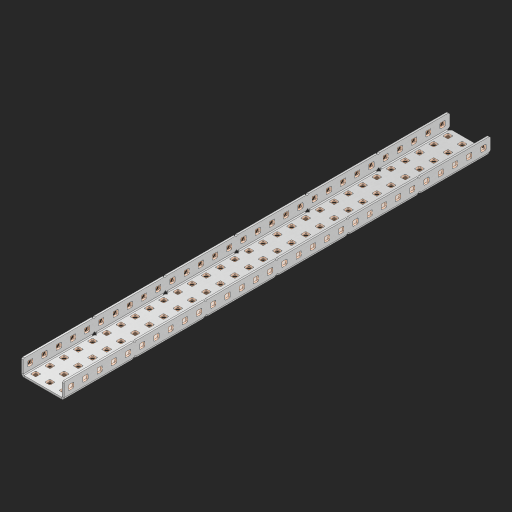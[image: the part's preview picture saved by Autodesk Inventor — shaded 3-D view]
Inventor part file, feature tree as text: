
AUTODESK INVENTOR PART (.ipt)
format: ipt  version: 2023 (Build 270158000, 158)  size: 1,831,424 bytes
history: native  units: in
note: dims shown in document units (in); Inventor stores cm internally (conversion verified against a paired STEP export)
features: other x155, extrude x149, sheet_metal_op x10, sketch x8, mirror x1, pattern_linear x1, chamfer x1
ambient origin geometry x8: Origin, YZ Plane, XZ Plane, XY Plane, X Axis, Y Axis, Z Axis, Center Point
bodies: Solid1 (feature_tree), Body (feature_tree)
feature tree (325):
  other  "Flange Pattern Plane"
  sheet_metal_op  "Flange Pattern"
  sheet_metal_op  "Body Pattern"
  other  "Arc Length"
  mirror  "Notch Mirror"
  pattern_linear  "Notch Pattern"  Spacing1=0.25in  [1 undecoded]
  chamfer  "End Chamfer"
  extrude  "Half Cut"  Depth=0.0625in
  sketch  "Sketch1"  dims[d0=1.5in]
  other  "Plate1"
  sketch  "Sketch2"  dims[d1=15.0in]
  other  "Plate2"
  sheet_metal_op  "Bend1"
  sheet_metal_op  "Corner1"
  sketch  "Sketch3"  dims[d2=0.0625in]
  other  "Flange Pattern Sketch"
  sketch  "Sketch7"  dims[d3=0.0625in]
  other  "Srf1"
  other  "Srf2"
  sketch  "Sketch8"  dims[d4=0.0312in]
  sketch  "Sketch9"  dims[d5=0.125in]
  other  "Srf91"
  sheet_metal_op  "Body Pattern Sketch"
  other  "Srf92"
  sketch  "Sketch13"  dims[d6=0.0625in]
  sketch  "Sketch14"  dims[d7=0.5in d8=90.0deg d9=0.0312in d10=0.25in d11=0.0625in d12=0.0625in d16=0.182in d17=0.02in d18=0.0625in d19=0.0in d20=0.25in d21=0.25in d46=0.172in d47=1.0in d48=0.0in d49=0.182in d50=0.02in d51=0.25in d52=0.25in d53=0.0625in d54=0.0in d55=0.172in d56=1.0in d57=0.0in d60=11.811in d62=0.5in d63=1.1811in d65=0.5in d85=0.1473in d86=0.1782in d88=0.04in d89=0.0625in d90=0.0in d91=0.04in d92=0.0491in d95=2.5in d96=0.04in d97=0.25in d98=45.0deg d101=0.0in d102=2.497in d131=1.5in d132=11.811in d134=0.5in d139=0.5in]
  other  "Srf856"
  other  "Srf1310"
  other  "Srf1311"
  other  "Srf1312"
  other  "Srf1376"
  other  "Srf1377"
  other  "Srf1728"
  other  "Srf1755"
  other  "Srf1878"
  other  "Srf1879"
  other  "Srf1880"
  other  "Srf1881"
  other  "Srf1882"
  other  "Srf1883"
  other  "Srf1884"
  other  "Srf1885"
  other  "Srf1886"
  other  "Srf1887"
  other  "Srf1888"
  other  "Srf1889"
  other  "Srf1890"
  other  "Srf1891"
  other  "Srf1892"
  other  "Srf1893"
  other  "Srf1894"
  other  "Srf1895"
  other  "Srf1896"
  other  "Srf1897"
  other  "Srf1898"
  other  "Srf1899"
  other  "Srf1900"
  other  "Srf1901"
  other  "Srf1902"
  other  "Srf1903"
  other  "Srf1904"
  other  "Srf1905"
  other  "Srf1906"
  other  "Srf1907"
  other  "Srf1908"
  other  "Srf1909"
  other  "Srf1910"
  other  "Srf1911"
  other  "Srf1912"
  other  "Srf1913"
  other  "Srf1914"
  other  "Srf1915"
  other  "Srf1916"
  other  "Srf1917"
  other  "Srf1918"
  other  "Srf1919"
  other  "Srf1920"
  other  "Srf1921"
  other  "Srf1922"
  other  "Srf1923"
  other  "Srf1924"
  other  "Srf1925"
  other  "Srf1926"
  other  "Srf1927"
  other  "Srf1928"
  other  "Srf1929"
  other  "Srf1930"
  other  "Srf1931"
  other  "Srf1942"
  other  "Srf1943"
  other  "Srf1944"
  other  "Srf1945"
  other  "Srf1946"
  other  "Srf1947"
  other  "Srf1948"
  other  "Srf1949"
  other  "Srf1950"
  other  "Srf1951"
  other  "Srf1952"
  other  "Srf1953"
  other  "Srf1954"
  other  "Srf1955"
  other  "Srf1956"
  other  "Srf1957"
  other  "Srf1958"
  other  "Srf1959"
  other  "Srf1960"
  other  "Srf1961"
  other  "Srf1962"
  other  "Srf1963"
  other  "Srf1964"
  other  "Srf1965"
  other  "Srf1966"
  other  "Srf1967"
  other  "Srf1968"
  other  "Srf1969"
  other  "Srf1970"
  other  "Srf1971"
  other  "Srf1972"
  other  "Srf1973"
  other  "Srf1974"
  other  "Srf1975"
  other  "Srf1976"
  other  "Srf1977"
  other  "Srf1978"
  other  "Srf1979"
  other  "Srf1980"
  other  "Srf1981"
  other  "Srf1982"
  other  "Srf1983"
  other  "Srf1984"
  other  "Srf1985"
  other  "Srf1986"
  other  "Srf1987"
  other  "Srf1988"
  other  "Srf1989"
  other  "Srf1990"
  other  "Srf1991"
  other  "Srf1992"
  other  "Srf1993"
  other  "Srf1994"
  other  "Srf1995"
  other  "Srf1996"
  other  "Srf1997"
  other  "Srf1998"
  other  "Srf1999"
  other  "Srf2000"
  other  "Srf2001"
  other  "Srf2002"
  other  "Srf2003"
  other  "Srf2004"
  other  "Srf2005"
  other  "Srf2006"
  other  "Srf2007"
  other  "Srf2008"
  other  "Srf2009"
  other  "Srf2010"
  other  "Srf2011"
  other  "Srf2012"
  other  "Srf2013"
  other  "Srf2014"
  other  "Srf2015"
  other  "Srf2016"
  other  "Srf2017"
  other  "Srf2018"
  other  "Srf2019"
  other  "Srf2020"
  other  "Srf2021"
  other  "Srf2022"
  other  "Srf2023"
  other  "Srf2024"
  other  "Srf2025"
  sheet_metal_op  "Flange Stamp"
  sheet_metal_op  "Flange Circle"
  sheet_metal_op  "Body Stamp"
  sheet_metal_op  "Body Circle"
  sheet_metal_op  "Notch"
  extrude  "ExtrusionSrf2"  Depth=0.0625in
  extrude  "ExtrusionSrf92"  Depth=1.5in
  extrude  "ExtrusionSrf856"  Depth=0.02in
  extrude  "ExtrusionSrf1310"  Depth=0.0625in
  extrude  "ExtrusionSrf1311"  TaperAngle=0.0deg  [1 undecoded]
  extrude  "ExtrusionSrf1312"  Depth=0.25in
  extrude  "ExtrusionSrf1376"  Depth=0.25in
  extrude  "ExtrusionSrf1377"  Depth=1.5in
  extrude  "ExtrusionSrf1728"  Depth=1.5in TaperAngle=0.0deg
  extrude  "ExtrusionSrf1755"  Depth=1.5in
  extrude  "ExtrusionSrf1878"  Depth=0.02in
  extrude  "ExtrusionSrf1879"  Depth=0.25in
  extrude  "ExtrusionSrf1880"  Depth=0.25in
  extrude  "ExtrusionSrf1881"  Depth=0.0625in
  extrude  "ExtrusionSrf1882"  TaperAngle=0.0deg  [1 undecoded]
  extrude  "ExtrusionSrf1883"  Depth=1.5in
  extrude  "ExtrusionSrf1884"  Depth=1.5in TaperAngle=0.0deg
  extrude  "ExtrusionSrf1885"  Depth=1.5in
  extrude  "ExtrusionSrf1886"  Depth=1.5in
  extrude  "ExtrusionSrf1887"  Depth=1.5in
  extrude  "ExtrusionSrf1888"  Depth=1.5in
  extrude  "ExtrusionSrf1889"  Depth=1.5in
  extrude  "ExtrusionSrf1890"  Depth=0.0625in
  extrude  "ExtrusionSrf1891"  TaperAngle=0.0deg  [1 undecoded]
  extrude  "ExtrusionSrf1892"  Depth=1.5in
  extrude  "ExtrusionSrf1893"  Depth=1.5in
  extrude  "ExtrusionSrf1894"  Depth=1.5in
  extrude  "ExtrusionSrf1895"  Depth=0.25in TaperAngle=45.0deg
  extrude  "ExtrusionSrf1896"  TaperAngle=0.0deg  [1 undecoded]
  extrude  "ExtrusionSrf1897"  Depth=1.5in
  extrude  "ExtrusionSrf1898"  Depth=1.5in
  extrude  "ExtrusionSrf1899"  Depth=1.5in
  extrude  "ExtrusionSrf1900"  Depth=1.5in
  extrude  "ExtrusionSrf1901"  Depth=1.5in
  extrude  "ExtrusionSrf1902"  [1 undecoded]
  extrude  "ExtrusionSrf1903"  [1 undecoded]
  extrude  "ExtrusionSrf1904"  [1 undecoded]
  extrude  "ExtrusionSrf1905"  [1 undecoded]
  extrude  "ExtrusionSrf1906"  [1 undecoded]
  extrude  "ExtrusionSrf1907"  [1 undecoded]
  extrude  "ExtrusionSrf1908"  [1 undecoded]
  extrude  "ExtrusionSrf1909"  [1 undecoded]
  extrude  "ExtrusionSrf1910"  [1 undecoded]
  extrude  "ExtrusionSrf1911"  [1 undecoded]
  extrude  "ExtrusionSrf1912"  [1 undecoded]
  extrude  "ExtrusionSrf1913"  [1 undecoded]
  extrude  "ExtrusionSrf1914"  [1 undecoded]
  extrude  "ExtrusionSrf1915"  [1 undecoded]
  extrude  "ExtrusionSrf1916"  [1 undecoded]
  extrude  "ExtrusionSrf1917"  [1 undecoded]
  extrude  "ExtrusionSrf1918"  [1 undecoded]
  extrude  "ExtrusionSrf1919"  [1 undecoded]
  extrude  "ExtrusionSrf1920"  [1 undecoded]
  extrude  "ExtrusionSrf1921"  [1 undecoded]
  extrude  "ExtrusionSrf1922"  [1 undecoded]
  extrude  "ExtrusionSrf1923"  [1 undecoded]
  extrude  "ExtrusionSrf1924"  [1 undecoded]
  extrude  "ExtrusionSrf1925"  [1 undecoded]
  extrude  "ExtrusionSrf1926"  [1 undecoded]
  extrude  "ExtrusionSrf1927"  [1 undecoded]
  extrude  "ExtrusionSrf1928"  [1 undecoded]
  extrude  "ExtrusionSrf1929"  [1 undecoded]
  extrude  "ExtrusionSrf1930"  [1 undecoded]
  extrude  "ExtrusionSrf1931"  [1 undecoded]
  extrude  "ExtrusionSrf1942"  [1 undecoded]
  extrude  "ExtrusionSrf1943"  [1 undecoded]
  extrude  "ExtrusionSrf1944"  [1 undecoded]
  extrude  "ExtrusionSrf1945"  [1 undecoded]
  extrude  "ExtrusionSrf1946"  [1 undecoded]
  extrude  "ExtrusionSrf1947"  [1 undecoded]
  extrude  "ExtrusionSrf1948"  [1 undecoded]
  extrude  "ExtrusionSrf1949"  [1 undecoded]
  extrude  "ExtrusionSrf1950"  [1 undecoded]
  extrude  "ExtrusionSrf1951"  [1 undecoded]
  extrude  "ExtrusionSrf1952"  [1 undecoded]
  extrude  "ExtrusionSrf1953"  [1 undecoded]
  extrude  "ExtrusionSrf1954"  [1 undecoded]
  extrude  "ExtrusionSrf1955"  [1 undecoded]
  extrude  "ExtrusionSrf1956"  [1 undecoded]
  extrude  "ExtrusionSrf1957"  [1 undecoded]
  extrude  "ExtrusionSrf1958"  [1 undecoded]
  extrude  "ExtrusionSrf1959"  [1 undecoded]
  extrude  "ExtrusionSrf1960"  [1 undecoded]
  extrude  "ExtrusionSrf1961"  [1 undecoded]
  extrude  "ExtrusionSrf1962"  [1 undecoded]
  extrude  "ExtrusionSrf1963"  [1 undecoded]
  extrude  "ExtrusionSrf1964"  [1 undecoded]
  extrude  "ExtrusionSrf1965"  [1 undecoded]
  extrude  "ExtrusionSrf1966"  [1 undecoded]
  extrude  "ExtrusionSrf1967"  [1 undecoded]
  extrude  "ExtrusionSrf1968"  [1 undecoded]
  extrude  "ExtrusionSrf1969"  [1 undecoded]
  extrude  "ExtrusionSrf1970"  [1 undecoded]
  extrude  "ExtrusionSrf1971"  [1 undecoded]
  extrude  "ExtrusionSrf1972"  [1 undecoded]
  extrude  "ExtrusionSrf1973"  [1 undecoded]
  extrude  "ExtrusionSrf1974"  [1 undecoded]
  extrude  "ExtrusionSrf1975"  [1 undecoded]
  extrude  "ExtrusionSrf1976"  [1 undecoded]
  extrude  "ExtrusionSrf1977"  [1 undecoded]
  extrude  "ExtrusionSrf1978"  [1 undecoded]
  extrude  "ExtrusionSrf1979"  [1 undecoded]
  extrude  "ExtrusionSrf1980"  [1 undecoded]
  extrude  "ExtrusionSrf1981"  [1 undecoded]
  extrude  "ExtrusionSrf1982"  [1 undecoded]
  extrude  "ExtrusionSrf1983"  [1 undecoded]
  extrude  "ExtrusionSrf1984"  [1 undecoded]
  extrude  "ExtrusionSrf1985"  [1 undecoded]
  extrude  "ExtrusionSrf1986"  [1 undecoded]
  extrude  "ExtrusionSrf1987"  [1 undecoded]
  extrude  "ExtrusionSrf1988"  [1 undecoded]
  extrude  "ExtrusionSrf1989"  [1 undecoded]
  extrude  "ExtrusionSrf1990"  [1 undecoded]
  extrude  "ExtrusionSrf1991"  [1 undecoded]
  extrude  "ExtrusionSrf1992"  [1 undecoded]
  extrude  "ExtrusionSrf1993"  [1 undecoded]
  extrude  "ExtrusionSrf1994"  [1 undecoded]
  extrude  "ExtrusionSrf1995"  [1 undecoded]
  extrude  "ExtrusionSrf1996"  [1 undecoded]
  extrude  "ExtrusionSrf1997"  [1 undecoded]
  extrude  "ExtrusionSrf1998"  [1 undecoded]
  extrude  "ExtrusionSrf1999"  [1 undecoded]
  extrude  "ExtrusionSrf2000"  [1 undecoded]
  extrude  "ExtrusionSrf2001"  [1 undecoded]
  extrude  "ExtrusionSrf2002"  [1 undecoded]
  extrude  "ExtrusionSrf2003"  [1 undecoded]
  extrude  "ExtrusionSrf2004"  [1 undecoded]
  extrude  "ExtrusionSrf2005"  [1 undecoded]
  extrude  "ExtrusionSrf2006"  [1 undecoded]
  extrude  "ExtrusionSrf2007"  [1 undecoded]
  extrude  "ExtrusionSrf2008"  [1 undecoded]
  extrude  "ExtrusionSrf2009"  [1 undecoded]
  extrude  "ExtrusionSrf2010"  [1 undecoded]
  extrude  "ExtrusionSrf2011"  [1 undecoded]
  extrude  "ExtrusionSrf2012"  [1 undecoded]
  extrude  "ExtrusionSrf2013"  [1 undecoded]
  extrude  "ExtrusionSrf2014"  [1 undecoded]
  extrude  "ExtrusionSrf2015"  [1 undecoded]
  extrude  "ExtrusionSrf2016"  [1 undecoded]
  extrude  "ExtrusionSrf2017"  [1 undecoded]
  extrude  "ExtrusionSrf2018"  [1 undecoded]
  extrude  "ExtrusionSrf2019"  [1 undecoded]
  extrude  "ExtrusionSrf2020"  [1 undecoded]
  extrude  "ExtrusionSrf2021"  [1 undecoded]
  extrude  "ExtrusionSrf2022"  [1 undecoded]
  extrude  "ExtrusionSrf2023"  [1 undecoded]
  extrude  "ExtrusionSrf2024"  [1 undecoded]
  extrude  "ExtrusionSrf2025"  [1 undecoded]
note: 119 required parameter values undecoded (feature->parameter linkage not recoverable at this tier; creation-order binding heuristic only, values carry confidence <= 0.55)
